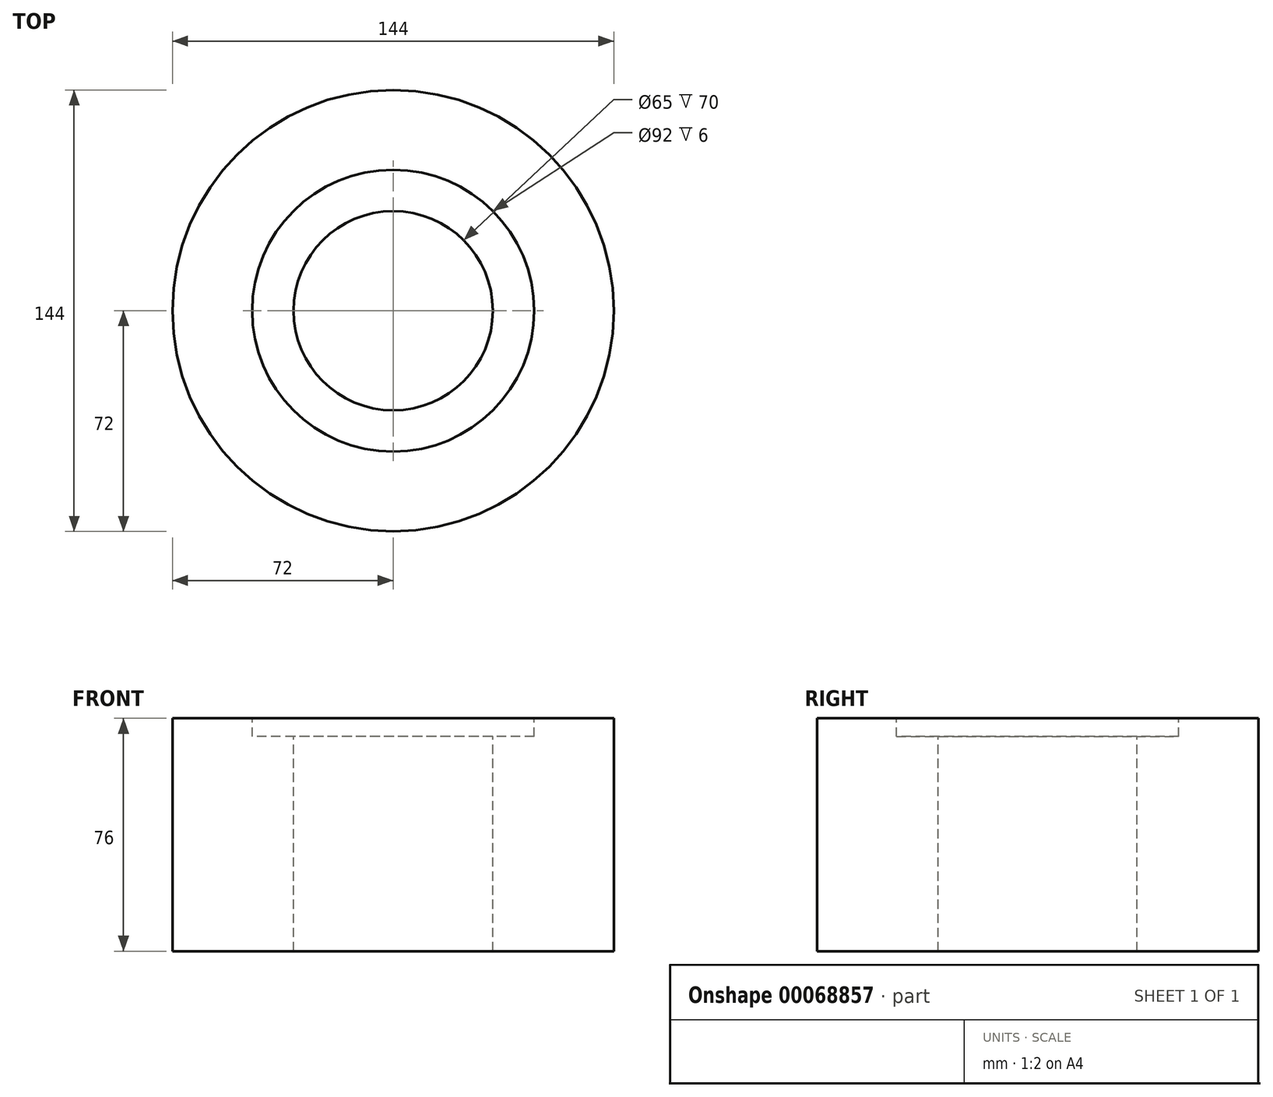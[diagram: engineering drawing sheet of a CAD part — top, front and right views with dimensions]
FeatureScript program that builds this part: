
annotation { "Feature Type Name" : "Feature", "Feature Type Description" : "" }
export const myFeature = defineFeature(function(context is Context, id is Id, definition is map)
    precondition{}
    {
        {
            var Q0;
            Q0=qCreatedBy(makeId("Top.planeOp"),FACE);
            var sketch = newSketch(context, id + "F0", { "sketchPlane" : qUnion([Q0])});
            skCircle(sketch, "E0", {"center": v(0, 0) * mm, "radius": 72 * mm});
            skSolve(sketch);
        }
        {
            var Q0;
            Q0 = qSketchRegion(id + "F0", true);
            extrude(context, id + "F1", {"entities" : qUnion([Q0]), "depth" : 76 * mm});
        }
        {
            var Q0;
            Q0=makeQuery(id+"F1.opExtrude","CAP_FACE",FACE,{"disambiguationData":[OSD([sQuery(id+"F0.wireOp",EDGE,"E0")])],"isStart":false});
            var sketch = newSketch(context, id + "F2", { "sketchPlane" : qUnion([Q0])});
            skPoint(sketch, "E1", {"position": v(0, 0) * mm});
            skSolve(sketch);
        }
        {
            var Q0;
            Q0=sQuery(id+"F2.wireOp",VERTEX,"E1");
            var Q1;
            Q1=makeQuery(id+"F1.opExtrude","SWEPT_BODY",BODY,{"disambiguationData":[OSD([sQuery(id+"F0.wireOp",EDGE,"E0")])]});
            hole(context, id + "F3", {"style" : HoleStyle.C_BORE, "holeDiameter" : 65 * mm, "cBoreDiameter" : 92 * mm, "cBoreDepth" : 6 * mm, "endStyle" : HoleEndStyle.THROUGH, "locations" : qUnion([Q0]), "scope" : qUnion([Q1])});
        }
    });
